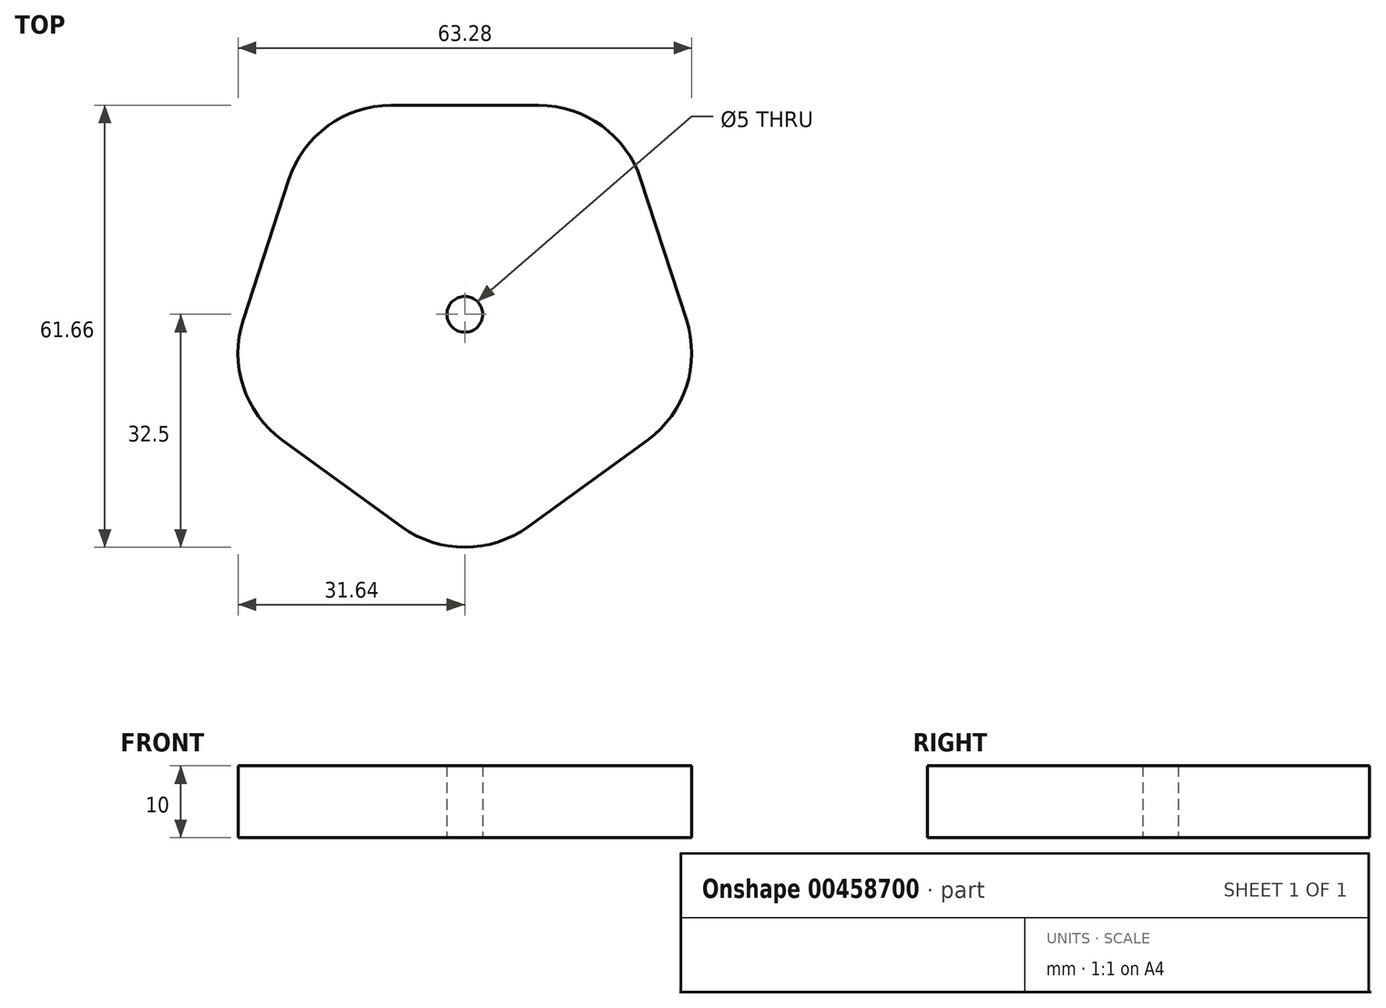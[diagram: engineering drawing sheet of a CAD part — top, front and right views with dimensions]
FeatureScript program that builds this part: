
annotation { "Feature Type Name" : "Feature", "Feature Type Description" : "" }
export const myFeature = defineFeature(function(context is Context, id is Id, definition is map)
    precondition{}
    {
        {
            var Q0;
            Q0=qCreatedBy(makeId("Top.planeOp"),FACE);
            var sketch = newSketch(context, id + "F0", { "sketchPlane" : qUnion([Q0])});
            skCircle(sketch, "E0.cCircle", {"center": v(0, 0) * mm, "radius": 29.16 * mm, "construction": true});
            skLineSegment(sketch, "E0.0", {"start": v(-10.29, 29.16) * mm, "end": v(10.29, 29.16) * mm});
            skLineSegment(sketch, "E0.1", {"start": v(24.55, 18.8) * mm, "end": v(30.9, -0.77) * mm});
            skLineSegment(sketch, "E0.2", {"start": v(25.46, -17.54) * mm, "end": v(8.82, -29.64) * mm});
            skLineSegment(sketch, "E0.3", {"start": v(-8.82, -29.64) * mm, "end": v(-25.46, -17.54) * mm});
            skLineSegment(sketch, "E0.4", {"start": v(-30.9, -0.77) * mm, "end": v(-24.55, 18.8) * mm});
            skPoint(sketch, "E0.0.midPoint", {"position": v(0, 29.16) * mm});
            skPoint(sketch, "E1.visualSharp", {"position": v(-21.18, 29.16) * mm});
            skArc(sketch, "E1.filletArc", {"start": v(-10.29, 29.16) * mm, "mid": v(-19.1, 26.3) * mm, "end": v(-24.55, 18.8) * mm});
            skPoint(sketch, "E2.visualSharp", {"position": v(-34.28, -11.14) * mm});
            skArc(sketch, "E2.filletArc", {"start": v(-30.9, -0.77) * mm, "mid": v(-30.9, -10.04) * mm, "end": v(-25.46, -17.54) * mm});
            skPoint(sketch, "E3.visualSharp", {"position": v(0, -36.04) * mm});
            skArc(sketch, "E3.filletArc", {"start": v(-8.82, -29.64) * mm, "mid": v(0, -32.5) * mm, "end": v(8.82, -29.64) * mm});
            skPoint(sketch, "E4.visualSharp", {"position": v(34.28, -11.14) * mm});
            skArc(sketch, "E4.filletArc", {"start": v(25.46, -17.54) * mm, "mid": v(30.9, -10.04) * mm, "end": v(30.9, -0.77) * mm});
            skPoint(sketch, "E5.visualSharp", {"position": v(21.18, 29.16) * mm});
            skArc(sketch, "E5.filletArc", {"start": v(24.55, 18.8) * mm, "mid": v(19.1, 26.3) * mm, "end": v(10.29, 29.16) * mm});
            skCircle(sketch, "E6", {"center": v(0, 0) * mm, "radius": 2.5 * mm});
            skSolve(sketch);
        }
        {
            var Q0;
            Q0 = qSketchRegion(id + "F0", true);
            extrude(context, id + "F1", {"entities" : qUnion([Q0]), "depth" : 10 * mm, "offsetDistance" : 25 * mm});
        }
    });
